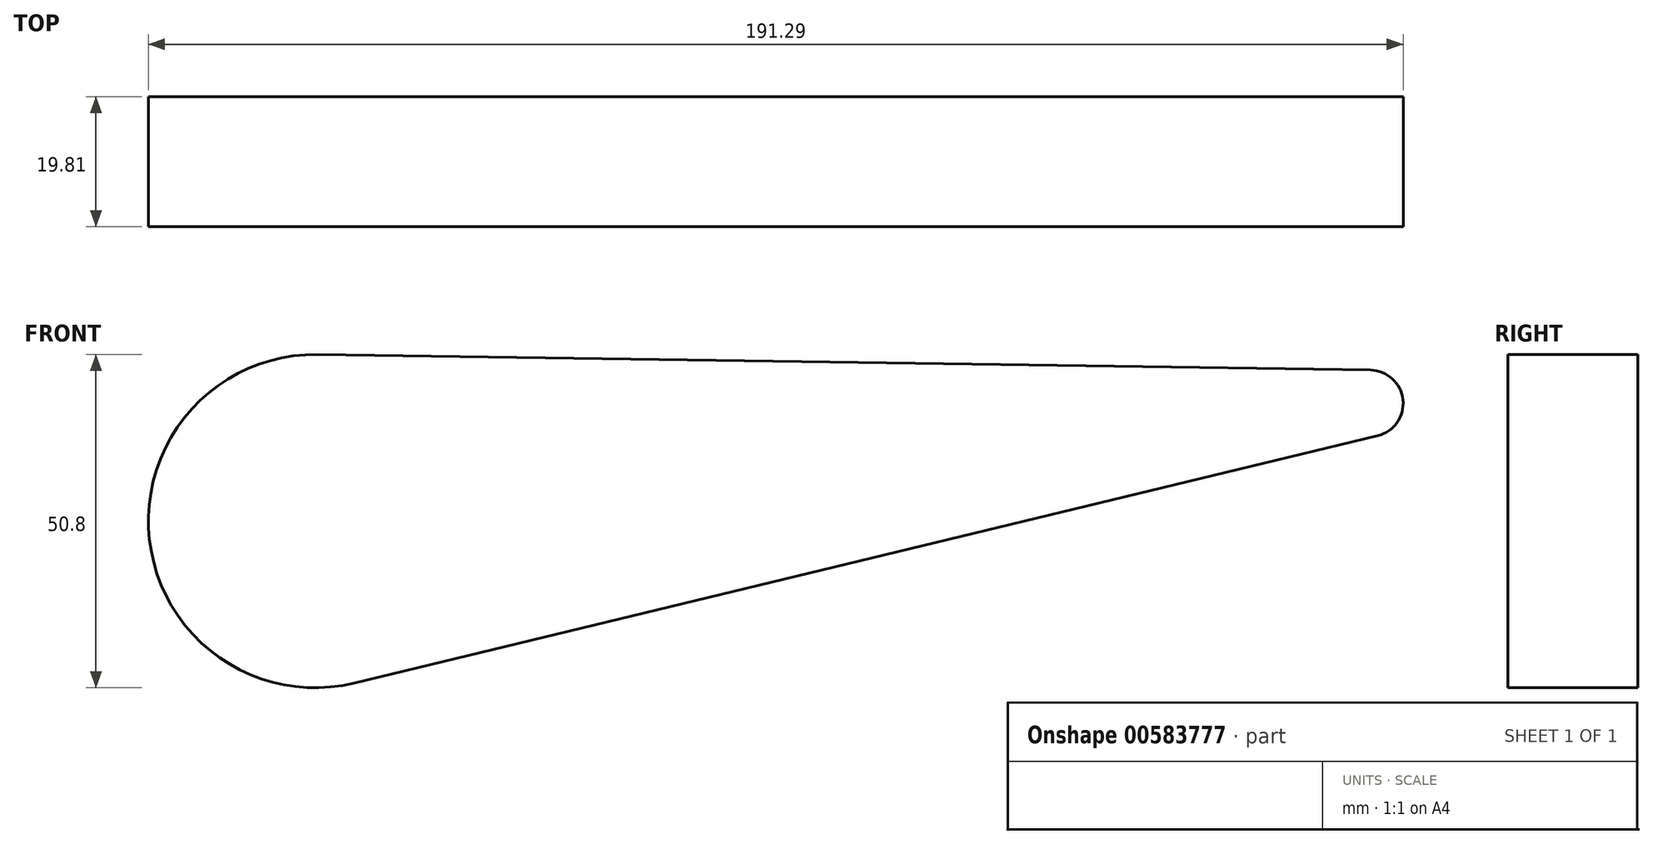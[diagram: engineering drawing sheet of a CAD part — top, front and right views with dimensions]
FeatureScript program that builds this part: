
annotation { "Feature Type Name" : "Feature", "Feature Type Description" : "" }
export const myFeature = defineFeature(function(context is Context, id is Id, definition is map)
    precondition{}
    {
        {
            var Q0;
            Q0=qCreatedBy(makeId("Front.planeOp"),FACE);
            var sketch = newSketch(context, id + "F0", { "sketchPlane" : qUnion([Q0])});
            skCircle(sketch, "E0", {"center": v(-89.38, -17.95) * mm, "radius": 25.4 * mm});
            skCircle(sketch, "E1", {"center": v(71.43, 0) * mm, "radius": 5.08 * mm});
            skLineSegment(sketch, "E2", {"start": v(-89, 7.45) * mm, "end": v(71.5, 5.08) * mm});
            skLineSegment(sketch, "E3", {"start": v(-83.42, -42.64) * mm, "end": v(72.63, -4.94) * mm});
            skSolve(sketch);
        }
        {
            var Q0;
            {var subQ0=sQuery(id+"F0.wireOp",EDGE,"E0");var subQ1=makeQuery(id+"F0.imprint","INTERSECT",VERTEX,{"derivedFrom":[subQ0,sQuery(id+"F0.wireOp",EDGE,"E2")]});Q0=makeQuery(id+"F0.imprint","IMPRINT",FACE,{"disambiguationData":[TD([[makeQuery(id+"F0.imprint","IMPRINT",EDGE,{"disambiguationData":[TD([[subQ1,-1.0]])],"derivedFrom":subQ0}),1.0]])]});}
            var Q1;
            {var subQ0=sQuery(id+"F0.wireOp",EDGE,"E2");Q1=makeQuery(id+"F0.imprint","IMPRINT",FACE,{"disambiguationData":[TD([[makeQuery(id+"F0.imprint","IMPRINT",EDGE,{"derivedFrom":subQ0}),-1.0]])]});}
            var Q2;
            {var subQ0=sQuery(id+"F0.wireOp",EDGE,"E1");var subQ1=makeQuery(id+"F0.imprint","INTERSECT",VERTEX,{"derivedFrom":[subQ0,sQuery(id+"F0.wireOp",EDGE,"E2")]});Q2=makeQuery(id+"F0.imprint","IMPRINT",FACE,{"disambiguationData":[TD([[makeQuery(id+"F0.imprint","IMPRINT",EDGE,{"disambiguationData":[TD([[subQ1,-1.0]])],"derivedFrom":subQ0}),1.0]])]});}
            extrude(context, id + "F1", {"entities" : qUnion([Q0, Q1, Q2]), "depth" : 19.8 * mm, "offsetDistance" : 25.4 * mm});
        }
    });
